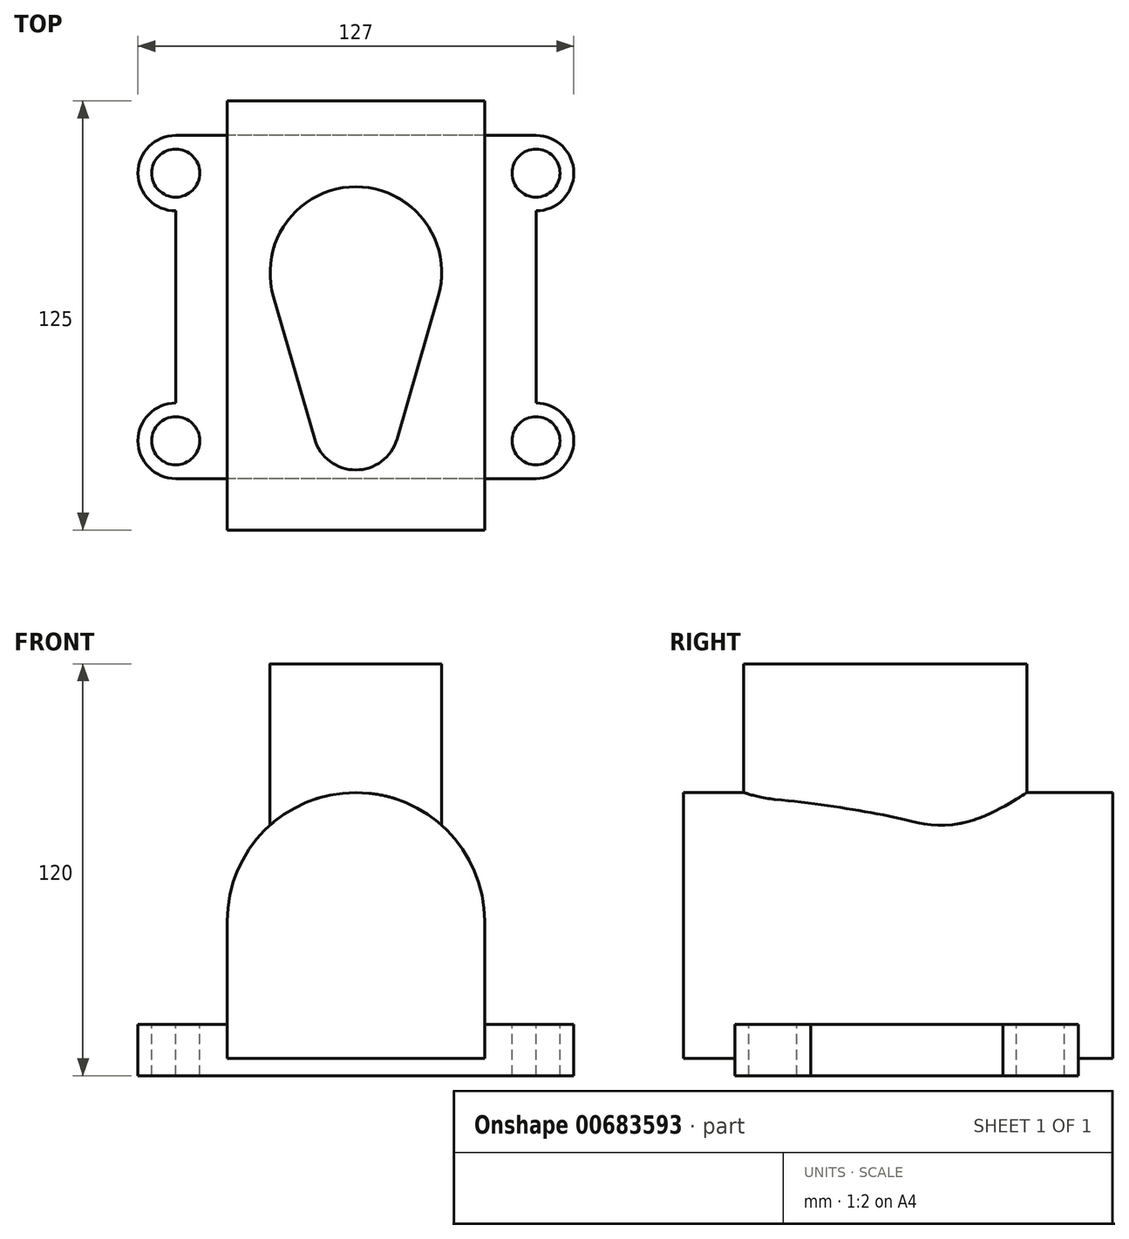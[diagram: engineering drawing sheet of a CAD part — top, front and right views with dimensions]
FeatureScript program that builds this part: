
annotation { "Feature Type Name" : "Feature", "Feature Type Description" : "" }
export const myFeature = defineFeature(function(context is Context, id is Id, definition is map)
    precondition{}
    {
        {
            var Q0;
            Q0=qCreatedBy(makeId("Front.planeOp"),FACE);
            var sketch = newSketch(context, id + "F0", { "sketchPlane" : qUnion([Q0])});
            skLineSegment(sketch, "E0", {"start": v(0, 65.92) * mm, "end": v(0, -70.05) * mm, "construction": true});
            skLineSegment(sketch, "E1", {"start": v(-86.62, 0) * mm, "end": v(100.1, 0) * mm, "construction": true});
            skLineSegment(sketch, "E2", {"start": v(-37.5, -40) * mm, "end": v(37.5, -40) * mm});
            skLineSegment(sketch, "E3", {"start": v(37.5, -40) * mm, "end": v(37.5, 0) * mm});
            skLineSegment(sketch, "E4", {"start": v(-37.5, -40) * mm, "end": v(-37.5, 0) * mm});
            skPoint(sketch, "E5", {"position": v(0, -40) * mm});
            skPoint(sketch, "E6", {"position": v(0, 70) * mm});
            skArc(sketch, "E7", {"start": v(37.5, 0) * mm, "mid": v(0, 37.5) * mm, "end": v(-37.5, 0) * mm});
            skSolve(sketch);
        }
        {
            var Q0;
            Q0 = qSketchRegion(id + "F0", true);
            var Q1;
            Q1=makeQuery(id+"F0.imprint","IMPRINT",FACE,{"disambiguationData":[TD([[makeQuery(id+"F0.imprint","IMPRINT",EDGE,{"derivedFrom":sQuery(id+"F0.wireOp",EDGE,"E2")}),1.0]])]});
            extrude(context, id + "F1", {"entities" : qUnion([Q0, Q1]), "depth" : 125 * mm, "offsetDistance" : 25 * mm});
        }
        {
            var Q0;
            Q0=makeQuery(id+"F1.opExtrude","SWEPT_FACE",FACE,{"disambiguationData":[OSD([sQuery(id+"F0.wireOp",EDGE,"E2")])]});
            var sketch = newSketch(context, id + "F2", { "sketchPlane" : qUnion([Q0])});
            skLineSegment(sketch, "E8.bottom", {"start": v(52.5, 110) * mm, "end": v(-52.5, 110) * mm});
            skLineSegment(sketch, "E8.top", {"start": v(52.5, 10) * mm, "end": v(-52.5, 10) * mm});
            skLineSegment(sketch, "E8.left", {"start": v(52.5, 110) * mm, "end": v(52.5, 10) * mm});
            skLineSegment(sketch, "E8.right", {"start": v(-52.5, 110) * mm, "end": v(-52.5, 10) * mm});
            skLineSegment(sketch, "E9", {"start": v(0, 125) * mm, "end": v(0, 0) * mm, "construction": true});
            skPoint(sketch, "E10", {"position": v(0, 110) * mm});
            skArc(sketch, "E11", {"start": v(52.5, 88) * mm, "mid": v(63.5, 99) * mm, "end": v(52.5, 110) * mm});
            skArc(sketch, "E12", {"start": v(52.5, 10) * mm, "mid": v(63.5, 21) * mm, "end": v(52.5, 32) * mm});
            skArc(sketch, "E13", {"start": v(-52.5, 110) * mm, "mid": v(-63.5, 99) * mm, "end": v(-52.5, 88) * mm});
            skArc(sketch, "E14", {"start": v(-52.5, 32) * mm, "mid": v(-63.5, 21) * mm, "end": v(-52.5, 10) * mm});
            skCircle(sketch, "E15", {"center": v(52.5, 99) * mm, "radius": 7 * mm});
            skCircle(sketch, "E16", {"center": v(52.5, 21) * mm, "radius": 7 * mm});
            skCircle(sketch, "E17", {"center": v(-52.5, 21) * mm, "radius": 7 * mm});
            skCircle(sketch, "E18", {"center": v(-52.5, 99) * mm, "radius": 7 * mm});
            skSolve(sketch);
        }
        {
            var Q0;
            Q0 = qSketchRegion(id + "F2", true);
            extrude(context, id + "F3", {"entities" : qUnion([Q0]), "operationType" : NewBodyOperationType.ADD, "depth" : 5 * mm, "offsetDistance" : 25 * mm, "hasSecondDirection" : true, "secondDirectionOppositeDirection" : true, "secondDirectionDepth" : 10 * mm});
        }
        {
            var Q0;
            Q0=qCreatedBy(makeId("Top.planeOp"),FACE);
            var sketch = newSketch(context, id + "F4", { "sketchPlane" : qUnion([Q0])});
            skLineSegment(sketch, "E19", {"start": v(0, 0) * mm, "end": v(0, -191.42) * mm, "construction": true});
            skLineSegment(sketch, "E20", {"start": v(-72.62, -50) * mm, "end": v(72.62, -50) * mm, "construction": true});
            skPoint(sketch, "E21", {"position": v(0, -50) * mm});
            skPoint(sketch, "E22", {"position": v(0, -95) * mm});
            skCircle(sketch, "E23", {"center": v(0, -95) * mm, "radius": 12.5 * mm, "construction": true});
            skCircle(sketch, "E24", {"center": v(0, -50) * mm, "radius": 25 * mm, "construction": true});
            skLineSegment(sketch, "E25", {"start": v(-12, -98.47) * mm, "end": v(-24.02, -56.94) * mm});
            skLineSegment(sketch, "E26", {"start": v(12, -98.47) * mm, "end": v(24.02, -56.94) * mm});
            skArc(sketch, "E27", {"start": v(-12, -98.47) * mm, "mid": v(0, -107.5) * mm, "end": v(12, -98.47) * mm});
            skArc(sketch, "E28", {"start": v(24.02, -56.94) * mm, "mid": v(0, -25) * mm, "end": v(-24.02, -56.94) * mm});
            skSolve(sketch);
        }
        {
            var Q0;
            Q0 = qSketchRegion(id + "F4", true);
            extrude(context, id + "F5", {"entities" : qUnion([Q0]), "operationType" : NewBodyOperationType.ADD, "depth" : 75 * mm, "offsetDistance" : 25 * mm});
        }
    });
